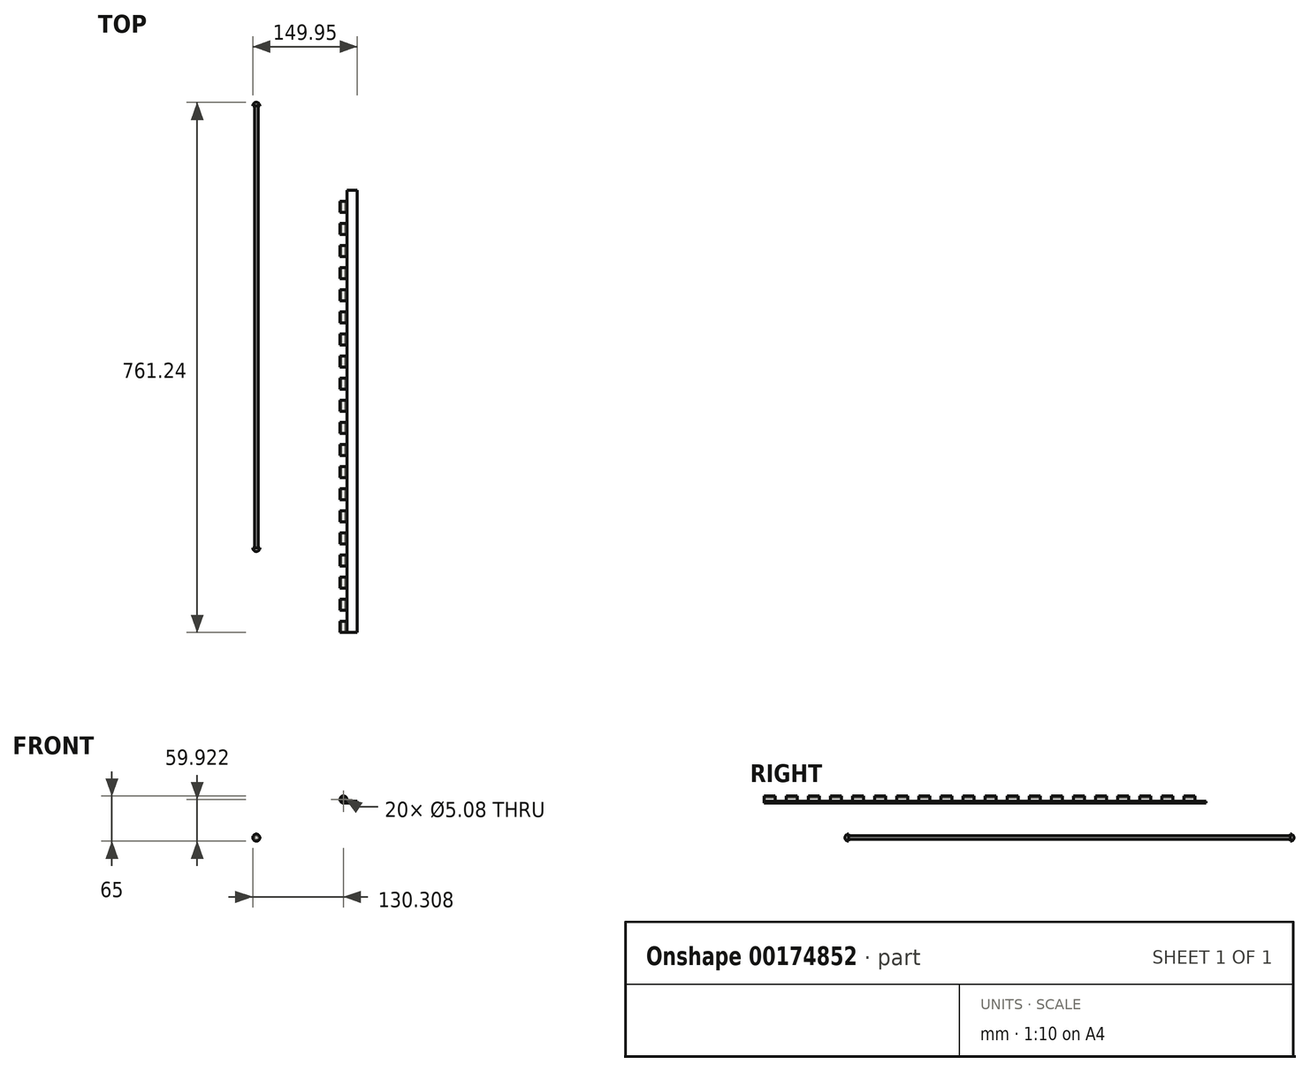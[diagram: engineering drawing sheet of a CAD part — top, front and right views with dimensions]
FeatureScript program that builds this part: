
annotation { "Feature Type Name" : "Feature", "Feature Type Description" : "" }
export const myFeature = defineFeature(function(context is Context, id is Id, definition is map)
    precondition{}
    {
        {
            var Q0;
            Q0=qCreatedBy(makeId("Front.planeOp"),FACE);
            var sketch = newSketch(context, id + "F0", { "sketchPlane" : qUnion([Q0])});
            skCircle(sketch, "E0", {"center": v(-17.02, 54.84) * mm, "radius": 5.08 * mm});
            skLineSegment(sketch, "E1", {"start": v(-17.02, 54.84) * mm, "end": v(-17.02, 21.28) * mm, "construction": true});
            skLineSegment(sketch, "E2", {"start": v(-17.02, 49.76) * mm, "end": v(2.62, 49.76) * mm});
            skLineSegment(sketch, "E3", {"start": v(2.62, 49.76) * mm, "end": v(2.62, 52.3) * mm});
            skLineSegment(sketch, "E4", {"start": v(2.62, 52.3) * mm, "end": v(-12.62, 52.3) * mm});
            skCircle(sketch, "E5", {"center": v(-17.02, 54.84) * mm, "radius": 2.54 * mm});
            skLineSegment(sketch, "E6", {"start": v(-12.62, 52.3) * mm, "end": v(-12.62, 68.46) * mm, "construction": true});
            skLineSegment(sketch, "E7", {"start": v(-17.02, 54.84) * mm, "end": v(18.39, 54.84) * mm});
            skPoint(sketch, "E8", {"position": v(-11.94, 54.84) * mm});
            skSolve(sketch);
        }
        {
            var Q0;
            Q0=qSketchRegion(id+"F0",true);
            extrude(context, id + "F1", {"entities" : qUnion([Q0]), "depth" : 635 * mm});
        }
        {
            var Q0;
            Q0=qCreatedBy(makeId("Top.planeOp"),FACE);
            var sketch = newSketch(context, id + "F2", { "sketchPlane" : qUnion([Q0])});
            skLineSegment(sketch, "E9.bottom", {"start": v(-24.64, 0) * mm, "end": v(-11.94, 0) * mm});
            skLineSegment(sketch, "E9.top", {"start": v(-24.64, -15.87) * mm, "end": v(-11.94, -15.87) * mm});
            skLineSegment(sketch, "E9.left", {"start": v(-24.64, 0) * mm, "end": v(-24.64, -15.87) * mm});
            skLineSegment(sketch, "E9.right", {"start": v(-11.94, 0) * mm, "end": v(-11.94, -15.87) * mm});
            skLineSegment(sketch, "E10.0.1.0", {"start": v(-24.64, -31.75) * mm, "end": v(-24.64, -47.63) * mm});
            skLineSegment(sketch, "E10.0.1.1", {"start": v(-24.64, -31.75) * mm, "end": v(-11.94, -31.75) * mm});
            skLineSegment(sketch, "E10.0.1.2", {"start": v(-24.64, -47.62) * mm, "end": v(-11.94, -47.62) * mm});
            skLineSegment(sketch, "E10.0.1.3", {"start": v(-11.94, -31.75) * mm, "end": v(-11.94, -47.62) * mm});
            skLineSegment(sketch, "E10.0.2.0", {"start": v(-24.64, -63.5) * mm, "end": v(-24.64, -79.37) * mm});
            skLineSegment(sketch, "E10.0.2.1", {"start": v(-24.64, -63.5) * mm, "end": v(-11.94, -63.5) * mm});
            skLineSegment(sketch, "E10.0.2.2", {"start": v(-24.64, -79.38) * mm, "end": v(-11.94, -79.38) * mm});
            skLineSegment(sketch, "E10.0.2.3", {"start": v(-11.94, -63.5) * mm, "end": v(-11.94, -79.37) * mm});
            skLineSegment(sketch, "E10.0.3.0", {"start": v(-24.64, -95.25) * mm, "end": v(-24.64, -111.13) * mm});
            skLineSegment(sketch, "E10.0.3.1", {"start": v(-24.64, -95.25) * mm, "end": v(-11.94, -95.25) * mm});
            skLineSegment(sketch, "E10.0.3.2", {"start": v(-24.64, -111.12) * mm, "end": v(-11.94, -111.12) * mm});
            skLineSegment(sketch, "E10.0.3.3", {"start": v(-11.94, -95.25) * mm, "end": v(-11.94, -111.12) * mm});
            skLineSegment(sketch, "E10.0.4.0", {"start": v(-24.64, -127) * mm, "end": v(-24.64, -142.87) * mm});
            skLineSegment(sketch, "E10.0.4.1", {"start": v(-24.64, -127) * mm, "end": v(-11.94, -127) * mm});
            skLineSegment(sketch, "E10.0.4.2", {"start": v(-24.64, -142.88) * mm, "end": v(-11.94, -142.88) * mm});
            skLineSegment(sketch, "E10.0.4.3", {"start": v(-11.94, -127) * mm, "end": v(-11.94, -142.87) * mm});
            skLineSegment(sketch, "E10.0.5.0", {"start": v(-24.64, -158.75) * mm, "end": v(-24.64, -174.63) * mm});
            skLineSegment(sketch, "E10.0.5.1", {"start": v(-24.64, -158.75) * mm, "end": v(-11.94, -158.75) * mm});
            skLineSegment(sketch, "E10.0.5.2", {"start": v(-24.64, -174.62) * mm, "end": v(-11.94, -174.62) * mm});
            skLineSegment(sketch, "E10.0.5.3", {"start": v(-11.94, -158.75) * mm, "end": v(-11.94, -174.62) * mm});
            skLineSegment(sketch, "E10.0.6.0", {"start": v(-24.64, -190.5) * mm, "end": v(-24.64, -206.37) * mm});
            skLineSegment(sketch, "E10.0.6.1", {"start": v(-24.64, -190.5) * mm, "end": v(-11.94, -190.5) * mm});
            skLineSegment(sketch, "E10.0.6.2", {"start": v(-24.64, -206.38) * mm, "end": v(-11.94, -206.38) * mm});
            skLineSegment(sketch, "E10.0.6.3", {"start": v(-11.94, -190.5) * mm, "end": v(-11.94, -206.37) * mm});
            skLineSegment(sketch, "E10.0.7.0", {"start": v(-24.64, -222.25) * mm, "end": v(-24.64, -238.13) * mm});
            skLineSegment(sketch, "E10.0.7.1", {"start": v(-24.64, -222.25) * mm, "end": v(-11.94, -222.25) * mm});
            skLineSegment(sketch, "E10.0.7.2", {"start": v(-24.64, -238.12) * mm, "end": v(-11.94, -238.12) * mm});
            skLineSegment(sketch, "E10.0.7.3", {"start": v(-11.94, -222.25) * mm, "end": v(-11.94, -238.12) * mm});
            skLineSegment(sketch, "E10.0.8.0", {"start": v(-24.64, -254) * mm, "end": v(-24.64, -269.88) * mm});
            skLineSegment(sketch, "E10.0.8.1", {"start": v(-24.64, -254) * mm, "end": v(-11.94, -254) * mm});
            skLineSegment(sketch, "E10.0.8.2", {"start": v(-24.64, -269.88) * mm, "end": v(-11.94, -269.88) * mm});
            skLineSegment(sketch, "E10.0.8.3", {"start": v(-11.94, -254) * mm, "end": v(-11.94, -269.88) * mm});
            skLineSegment(sketch, "E10.0.9.0", {"start": v(-24.64, -285.75) * mm, "end": v(-24.64, -301.63) * mm});
            skLineSegment(sketch, "E10.0.9.1", {"start": v(-24.64, -285.75) * mm, "end": v(-11.94, -285.75) * mm});
            skLineSegment(sketch, "E10.0.9.2", {"start": v(-24.64, -301.62) * mm, "end": v(-11.94, -301.62) * mm});
            skLineSegment(sketch, "E10.0.9.3", {"start": v(-11.94, -285.75) * mm, "end": v(-11.94, -301.62) * mm});
            skLineSegment(sketch, "E10.0.10.0", {"start": v(-24.64, -317.5) * mm, "end": v(-24.64, -333.38) * mm});
            skLineSegment(sketch, "E10.0.10.1", {"start": v(-24.64, -317.5) * mm, "end": v(-11.94, -317.5) * mm});
            skLineSegment(sketch, "E10.0.10.2", {"start": v(-24.64, -333.38) * mm, "end": v(-11.94, -333.38) * mm});
            skLineSegment(sketch, "E10.0.10.3", {"start": v(-11.94, -317.5) * mm, "end": v(-11.94, -333.38) * mm});
            skLineSegment(sketch, "E10.0.11.0", {"start": v(-24.64, -349.25) * mm, "end": v(-24.64, -365.12) * mm});
            skLineSegment(sketch, "E10.0.11.1", {"start": v(-24.64, -349.25) * mm, "end": v(-11.94, -349.25) * mm});
            skLineSegment(sketch, "E10.0.11.2", {"start": v(-24.64, -365.12) * mm, "end": v(-11.94, -365.12) * mm});
            skLineSegment(sketch, "E10.0.11.3", {"start": v(-11.94, -349.25) * mm, "end": v(-11.94, -365.12) * mm});
            skLineSegment(sketch, "E10.direction1", {"start": v(-24.64, -15.87) * mm, "end": v(102.36, -15.87) * mm, "construction": true});
            skLineSegment(sketch, "E10.direction2", {"start": v(-24.64, -15.87) * mm, "end": v(-24.64, -47.62) * mm, "construction": true});
            skLineSegment(sketch, "E11.0.0.12", {"start": v(-24.64, -381) * mm, "end": v(-24.64, -396.88) * mm});
            skLineSegment(sketch, "E11.3.0.12", {"start": v(-24.64, -381) * mm, "end": v(-11.94, -381) * mm});
            skLineSegment(sketch, "E11.6.0.12", {"start": v(-24.64, -396.88) * mm, "end": v(-11.94, -396.88) * mm});
            skLineSegment(sketch, "E11.9.0.12", {"start": v(-11.94, -381) * mm, "end": v(-11.94, -396.88) * mm});
            skLineSegment(sketch, "E12.0.0.13", {"start": v(-24.64, -412.75) * mm, "end": v(-24.64, -428.63) * mm});
            skLineSegment(sketch, "E12.3.0.13", {"start": v(-24.64, -412.75) * mm, "end": v(-11.94, -412.75) * mm});
            skLineSegment(sketch, "E12.6.0.13", {"start": v(-24.64, -428.62) * mm, "end": v(-11.94, -428.62) * mm});
            skLineSegment(sketch, "E12.9.0.13", {"start": v(-11.94, -412.75) * mm, "end": v(-11.94, -428.62) * mm});
            skLineSegment(sketch, "E12.0.0.14", {"start": v(-24.64, -444.5) * mm, "end": v(-24.64, -460.38) * mm});
            skLineSegment(sketch, "E12.3.0.14", {"start": v(-24.64, -444.5) * mm, "end": v(-11.94, -444.5) * mm});
            skLineSegment(sketch, "E12.6.0.14", {"start": v(-24.64, -460.38) * mm, "end": v(-11.94, -460.38) * mm});
            skLineSegment(sketch, "E12.9.0.14", {"start": v(-11.94, -444.5) * mm, "end": v(-11.94, -460.38) * mm});
            skLineSegment(sketch, "E12.0.0.15", {"start": v(-24.64, -476.25) * mm, "end": v(-24.64, -492.12) * mm});
            skLineSegment(sketch, "E12.3.0.15", {"start": v(-24.64, -476.25) * mm, "end": v(-11.94, -476.25) * mm});
            skLineSegment(sketch, "E12.6.0.15", {"start": v(-24.64, -492.12) * mm, "end": v(-11.94, -492.12) * mm});
            skLineSegment(sketch, "E12.9.0.15", {"start": v(-11.94, -476.25) * mm, "end": v(-11.94, -492.12) * mm});
            skLineSegment(sketch, "E12.0.0.16", {"start": v(-24.64, -508) * mm, "end": v(-24.64, -523.88) * mm});
            skLineSegment(sketch, "E12.3.0.16", {"start": v(-24.64, -508) * mm, "end": v(-11.94, -508) * mm});
            skLineSegment(sketch, "E12.6.0.16", {"start": v(-24.64, -523.88) * mm, "end": v(-11.94, -523.88) * mm});
            skLineSegment(sketch, "E12.9.0.16", {"start": v(-11.94, -508) * mm, "end": v(-11.94, -523.88) * mm});
            skLineSegment(sketch, "E12.0.0.17", {"start": v(-24.64, -539.75) * mm, "end": v(-24.64, -555.62) * mm});
            skLineSegment(sketch, "E12.3.0.17", {"start": v(-24.64, -539.75) * mm, "end": v(-11.94, -539.75) * mm});
            skLineSegment(sketch, "E12.6.0.17", {"start": v(-24.64, -555.62) * mm, "end": v(-11.94, -555.62) * mm});
            skLineSegment(sketch, "E12.9.0.17", {"start": v(-11.94, -539.75) * mm, "end": v(-11.94, -555.62) * mm});
            skLineSegment(sketch, "E12.0.0.18", {"start": v(-24.64, -571.5) * mm, "end": v(-24.64, -587.38) * mm});
            skLineSegment(sketch, "E12.3.0.18", {"start": v(-24.64, -571.5) * mm, "end": v(-11.94, -571.5) * mm});
            skLineSegment(sketch, "E12.6.0.18", {"start": v(-24.64, -587.38) * mm, "end": v(-11.94, -587.38) * mm});
            skLineSegment(sketch, "E12.9.0.18", {"start": v(-11.94, -571.5) * mm, "end": v(-11.94, -587.38) * mm});
            skLineSegment(sketch, "E12.0.0.19", {"start": v(-24.64, -603.25) * mm, "end": v(-24.64, -619.12) * mm});
            skLineSegment(sketch, "E12.3.0.19", {"start": v(-24.64, -603.25) * mm, "end": v(-11.94, -603.25) * mm});
            skLineSegment(sketch, "E12.6.0.19", {"start": v(-24.64, -619.12) * mm, "end": v(-11.94, -619.12) * mm});
            skLineSegment(sketch, "E12.9.0.19", {"start": v(-11.94, -603.25) * mm, "end": v(-11.94, -619.12) * mm});
            skSolve(sketch);
        }
        {
            var Q0;
            Q0=qSketchRegion(id+"F2",true);
            extrude(context, id + "F3", {"entities" : qUnion([Q0]), "operationType" : NewBodyOperationType.REMOVE, "depth" : 127 * mm});
        }
        {
            var Q0;
            Q0=qCreatedBy(makeId("Top.planeOp"),FACE);
            var sketch = newSketch(context, id + "F4", { "sketchPlane" : qUnion([Q0])});
            skLineSegment(sketch, "E13", {"start": v(-142.25, 121.16) * mm, "end": v(-139.71, 121.16) * mm});
            skLineSegment(sketch, "E14", {"start": v(-139.71, 121.16) * mm, "end": v(-139.71, -513.84) * mm});
            skLineSegment(sketch, "E15", {"start": v(-139.71, -513.84) * mm, "end": v(-142.25, -513.84) * mm});
            skLineSegment(sketch, "E16", {"start": v(-142.25, -513.84) * mm, "end": v(-142.25, 121.16) * mm});
            skLineSegment(sketch, "E17", {"start": v(-139.71, -513.84) * mm, "end": v(-137.17, -513.84) * mm});
            skArc(sketch, "E18", {"start": v(-137.17, -513.84) * mm, "mid": v(-138.66, -517.43) * mm, "end": v(-142.25, -518.92) * mm});
            skLineSegment(sketch, "E19", {"start": v(-142.25, -513.84) * mm, "end": v(-142.25, -518.92) * mm});
            skLineSegment(sketch, "E20", {"start": v(-139.71, 121.16) * mm, "end": v(-137.17, 121.16) * mm});
            skArc(sketch, "E21", {"start": v(-137.17, 121.16) * mm, "mid": v(-138.66, 124.75) * mm, "end": v(-142.25, 126.24) * mm});
            skLineSegment(sketch, "E22", {"start": v(-142.25, 121.16) * mm, "end": v(-142.25, 126.24) * mm});
            skSolve(sketch);
        }
        {
            var Q0;
            Q0=qSketchRegion(id+"F4",true);
            var Q1;
            Q1=sQuery(id+"F4.wireOp",EDGE,"E16");
            revolve(context, id + "F5", {"entities" : qUnion([Q0]), "axis" : qUnion([Q1]), "revolveType" : RevolveType.FULL});
        }
    });
